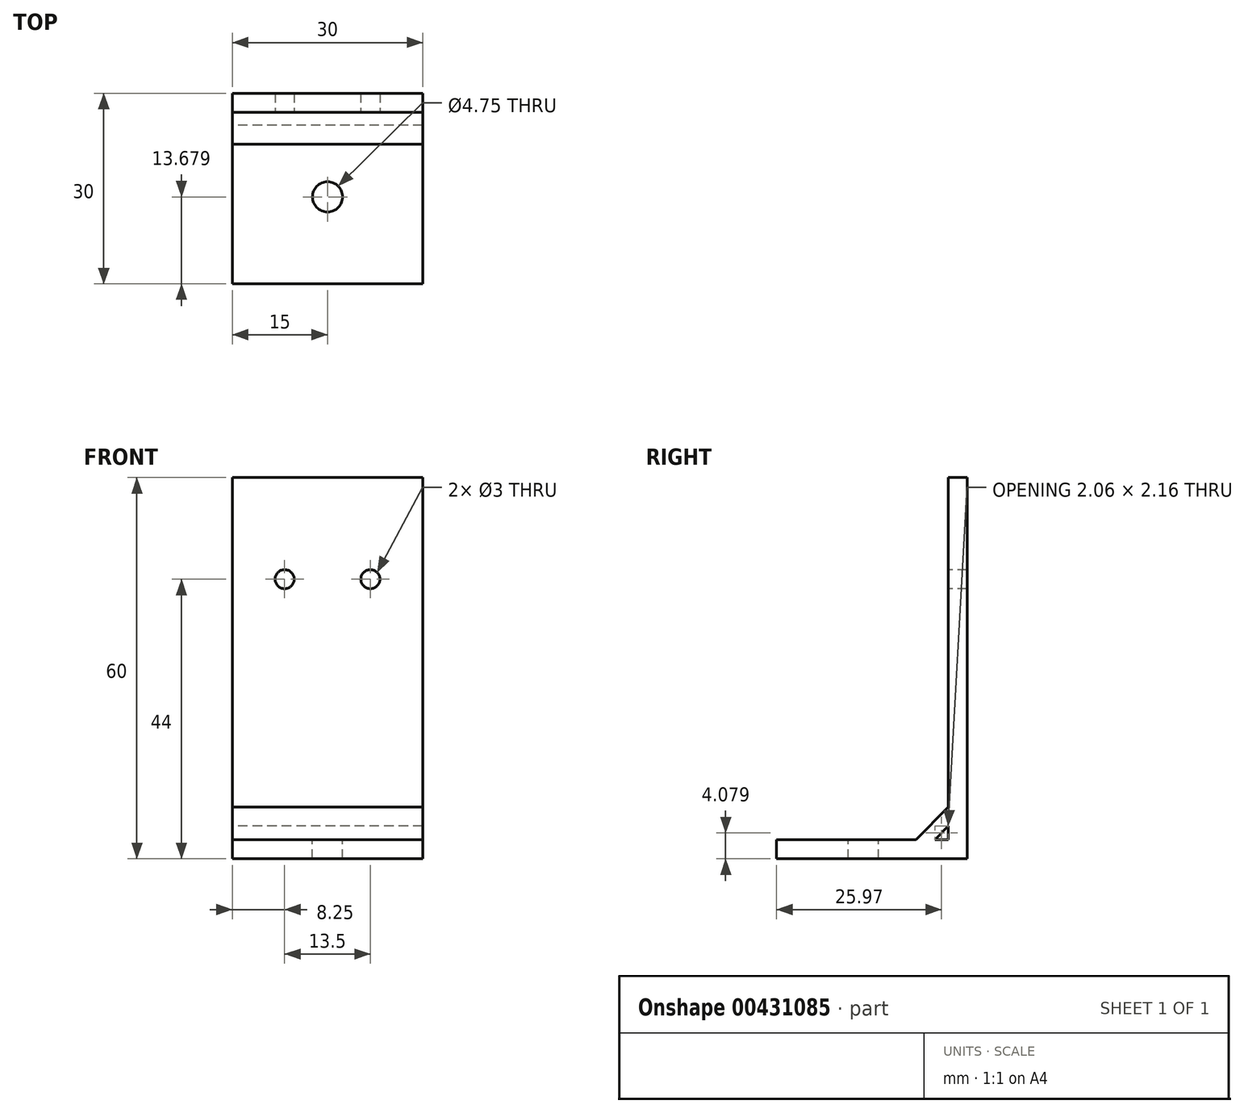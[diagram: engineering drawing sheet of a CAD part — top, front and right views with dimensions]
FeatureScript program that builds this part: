
annotation { "Feature Type Name" : "Feature", "Feature Type Description" : "" }
export const myFeature = defineFeature(function(context is Context, id is Id, definition is map)
    precondition{}
    {
        {
            var Q0;
            Q0=qCreatedBy(makeId("Top.planeOp"),FACE);
            var sketch = newSketch(context, id + "F0", { "sketchPlane" : qUnion([Q0])});
            skLineSegment(sketch, "E0.bottom", {"start": v(15, -15) * mm, "end": v(-15, -15) * mm});
            skLineSegment(sketch, "E0.top", {"start": v(15, 15) * mm, "end": v(-15, 15) * mm});
            skLineSegment(sketch, "E0.left", {"start": v(15, -15) * mm, "end": v(15, 15) * mm});
            skLineSegment(sketch, "E0.right", {"start": v(-15, -15) * mm, "end": v(-15, 15) * mm});
            skPoint(sketch, "E0.middle", {"position": v(0, 0) * mm});
            skSolve(sketch);
        }
        {
            var Q0;
            Q0=makeQuery(id+"F0.imprint","IMPRINT",FACE,{"disambiguationData":[TD([[makeQuery(id+"F0.imprint","IMPRINT",EDGE,{"derivedFrom":sQuery(id+"F0.wireOp",EDGE,"E0.bottom")}),-1.0]])]});
            extrude(context, id + "F1", {"entities" : qUnion([Q0]), "depth" : 3 * mm});
        }
        {
            var Q0;
            Q0=makeQuery(id+"F1.opExtrude","CAP_FACE",FACE,{"disambiguationData":[OSD([sQuery(id+"F0.wireOp",EDGE,"E0.bottom"),sQuery(id+"F0.wireOp",EDGE,"E0.top"),sQuery(id+"F0.wireOp",EDGE,"E0.left"),sQuery(id+"F0.wireOp",EDGE,"E0.right")])],"isStart":false});
            var sketch = newSketch(context, id + "F2", { "sketchPlane" : qUnion([Q0])});
            skLineSegment(sketch, "E1.bottom", {"start": v(-15, 15) * mm, "end": v(15, 15) * mm});
            skLineSegment(sketch, "E1.top", {"start": v(-15, 12) * mm, "end": v(15, 12) * mm});
            skLineSegment(sketch, "E1.left", {"start": v(-15, 15) * mm, "end": v(-15, 12) * mm});
            skLineSegment(sketch, "E1.right", {"start": v(15, 15) * mm, "end": v(15, 12) * mm});
            skSolve(sketch);
        }
        {
            var Q0;
            Q0=makeQuery(id+"F2.imprint","IMPRINT",FACE,{"disambiguationData":[TD([[makeQuery(id+"F2.imprint","IMPRINT",EDGE,{"derivedFrom":sQuery(id+"F2.wireOp",EDGE,"E1.bottom")}),1.0]])]});
            extrude(context, id + "F3", {"entities" : qUnion([Q0]), "operationType" : NewBodyOperationType.ADD, "depth" : 57 * mm});
        }
        {
            var Q0;
            Q0=makeQuery(id+"F1.opExtrude","CAP_FACE",FACE,{"disambiguationData":[OSD([sQuery(id+"F0.wireOp",EDGE,"E0.bottom"),sQuery(id+"F0.wireOp",EDGE,"E0.top"),sQuery(id+"F0.wireOp",EDGE,"E0.left"),sQuery(id+"F0.wireOp",EDGE,"E0.right")])],"isStart":false});
            var sketch = newSketch(context, id + "F4", { "sketchPlane" : qUnion([Q0])});
            skCircle(sketch, "E2", {"center": v(0, -1.32) * mm, "radius": 2.38 * mm});
            skSolve(sketch);
        }
        {
            var Q0;
            Q0=makeQuery(id+"F4.imprint","IMPRINT",FACE,{"disambiguationData":[TD([[makeQuery(id+"F4.imprint","IMPRINT",EDGE,{"derivedFrom":sQuery(id+"F4.wireOp",EDGE,"E2")}),1.0]])]});
            extrude(context, id + "F5", {"entities" : qUnion([Q0]), "operationType" : NewBodyOperationType.REMOVE, "endBound" : BoundingType.UP_TO_NEXT, "oppositeDirection" : true, "depth" : 25 * mm});
        }
        {
            var Q0;
            Q0=makeQuery(id+"F3.opExtrude","SWEPT_FACE",FACE,{"disambiguationData":[OSD([sQuery(id+"F2.wireOp",EDGE,"E1.top")])]});
            var sketch = newSketch(context, id + "F6", { "sketchPlane" : qUnion([Q0])});
            skCircle(sketch, "E3", {"center": v(-6.75, 44) * mm, "radius": 1.5 * mm});
            skCircle(sketch, "E4", {"center": v(6.75, 44) * mm, "radius": 1.5 * mm});
            skLineSegment(sketch, "E5", {"start": v(-6.75, 44) * mm, "end": v(0, 44) * mm});
            skLineSegment(sketch, "E6", {"start": v(0, 44) * mm, "end": v(6.75, 44) * mm});
            skSolve(sketch);
        }
        {
            var Q0;
            Q0=makeQuery(id+"F6.imprint","IMPRINT",FACE,{"disambiguationData":[TD([[makeQuery(id+"F6.imprint","IMPRINT",EDGE,{"derivedFrom":sQuery(id+"F6.wireOp",EDGE,"E3")}),1.0]])]});
            var Q1;
            Q1=makeQuery(id+"F6.imprint","IMPRINT",FACE,{"disambiguationData":[TD([[makeQuery(id+"F6.imprint","IMPRINT",EDGE,{"derivedFrom":sQuery(id+"F6.wireOp",EDGE,"E4")}),1.0]])]});
            extrude(context, id + "F7", {"entities" : qUnion([Q0, Q1]), "operationType" : NewBodyOperationType.REMOVE, "endBound" : BoundingType.UP_TO_NEXT, "oppositeDirection" : true, "depth" : 25 * mm});
        }
        {
            var Q0;
            Q0=makeQuery(id+"F3.boolean.opBoolean","MERGE",FACE,{"derivedFrom":[makeQuery(id+"F1.opExtrude","SWEPT_FACE",FACE,{"disambiguationData":[OSD([sQuery(id+"F0.wireOp",EDGE,"E0.right")])]}),makeQuery(id+"F3.opExtrude","SWEPT_FACE",FACE,{"disambiguationData":[OSD([sQuery(id+"F2.wireOp",EDGE,"E1.left")])]})]});
            cPlane(context, id + "F8", {"entities" : qUnion([Q0]), "cplaneType" : CPlaneType.OFFSET, "offset" : 0 * mm, "width" : 150 * mm, "height" : 150 * mm});
        }
        {
            var Q0;
            Q0=qCreatedBy(id+"F8.planeOp",FACE);
            var sketch = newSketch(context, id + "F9", { "sketchPlane" : qUnion([Q0])});
            skLineSegment(sketch, "E7", {"start": v(-9.94, 3) * mm, "end": v(-6.94, 3) * mm});
            skLineSegment(sketch, "E8", {"start": v(-6.94, 3) * mm, "end": v(-12, 8.16) * mm});
            skLineSegment(sketch, "E9", {"start": v(-12, 8.16) * mm, "end": v(-12, 5.16) * mm});
            skLineSegment(sketch, "E10", {"start": v(-12, 5.16) * mm, "end": v(-9.94, 3) * mm});
            skSolve(sketch);
        }
        {
            var Q0;
            Q0=makeQuery(id+"F9.imprint","IMPRINT",FACE,{"disambiguationData":[TD([[makeQuery(id+"F9.imprint","IMPRINT",EDGE,{"derivedFrom":sQuery(id+"F9.wireOp",EDGE,"E7")}),1.0]])]});
            var Q1;
            Q1=makeQuery(id+"F3.boolean.opBoolean","MERGE",FACE,{"derivedFrom":[makeQuery(id+"F1.opExtrude","SWEPT_FACE",FACE,{"disambiguationData":[OSD([sQuery(id+"F0.wireOp",EDGE,"E0.left")])]}),makeQuery(id+"F3.opExtrude","SWEPT_FACE",FACE,{"disambiguationData":[OSD([sQuery(id+"F2.wireOp",EDGE,"E1.right")])]})]});
            extrude(context, id + "F10", {"entities" : qUnion([Q0]), "operationType" : NewBodyOperationType.ADD, "endBound" : BoundingType.UP_TO_SURFACE, "oppositeDirection" : true, "endBoundEntityFace" : qUnion([Q1]), "depth" : 25 * mm});
        }
    });
